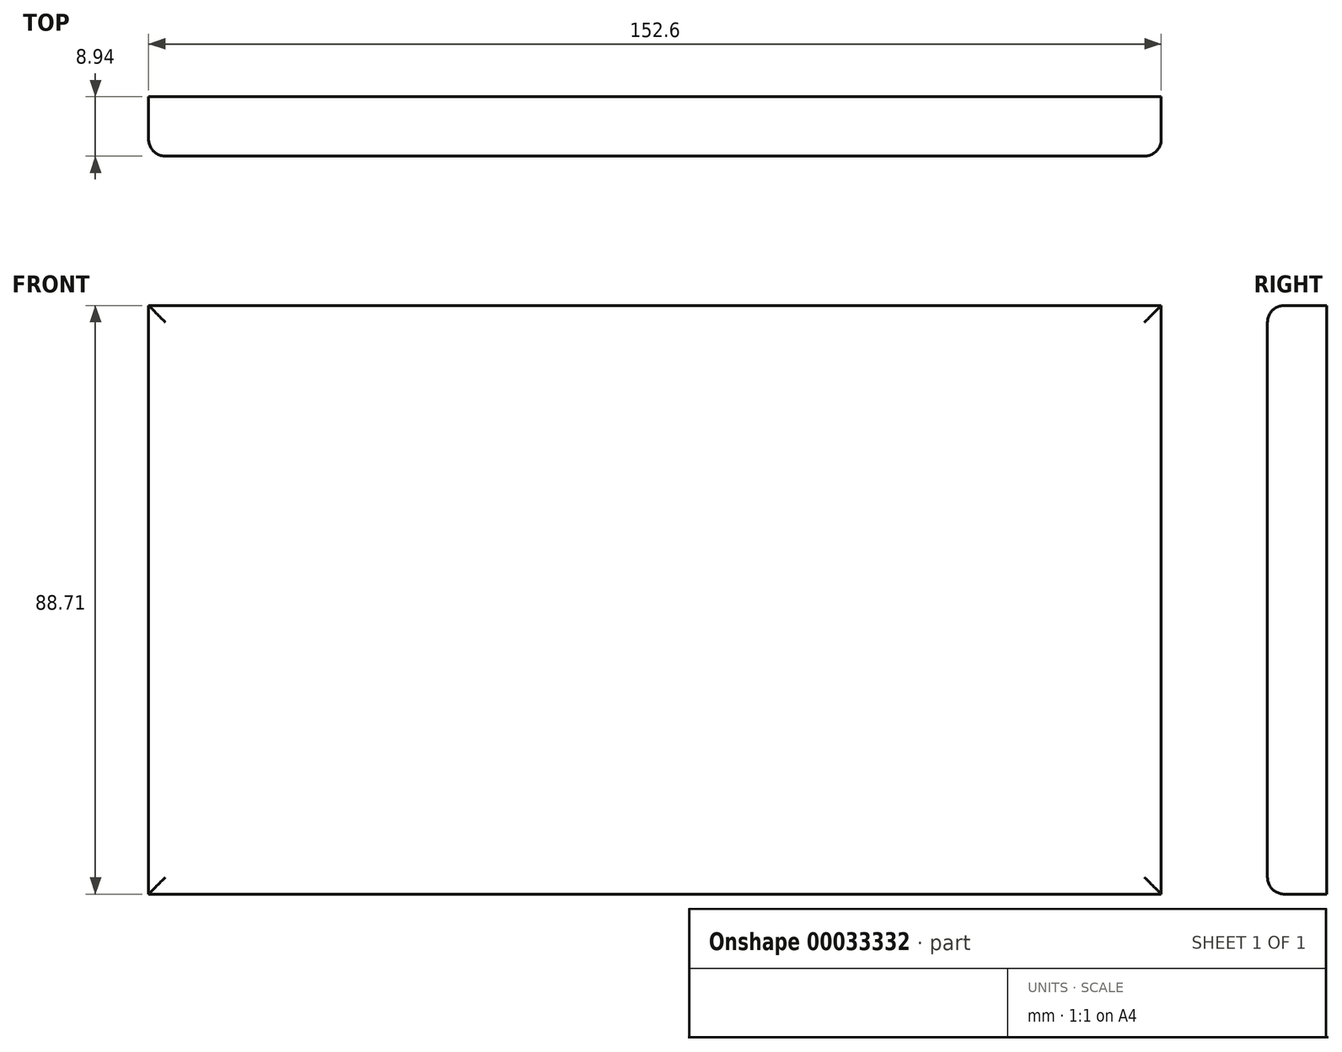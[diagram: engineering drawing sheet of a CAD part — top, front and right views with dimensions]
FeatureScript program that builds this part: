
annotation { "Feature Type Name" : "Feature", "Feature Type Description" : "" }
export const myFeature = defineFeature(function(context is Context, id is Id, definition is map)
    precondition{}
    {
        {
            var Q0;
            Q0=qCreatedBy(makeId("Front.planeOp"),FACE);
            var sketch = newSketch(context, id + "F0", { "sketchPlane" : qUnion([Q0])});
            skLineSegment(sketch, "E0.bottom", {"start": v(-76.44, 47.2) * mm, "end": v(76.16, 47.2) * mm});
            skLineSegment(sketch, "E0.top", {"start": v(-76.44, -41.5) * mm, "end": v(76.16, -41.5) * mm});
            skLineSegment(sketch, "E0.left", {"start": v(-76.44, 47.2) * mm, "end": v(-76.44, -41.5) * mm});
            skLineSegment(sketch, "E0.right", {"start": v(76.16, 47.2) * mm, "end": v(76.16, -41.5) * mm});
            skSolve(sketch);
        }
        {
            var Q0;
            Q0=makeQuery(id+"F0.imprint","IMPRINT",FACE,{"disambiguationData":[TD([[makeQuery(id+"F0.imprint","IMPRINT",EDGE,{"derivedFrom":sQuery(id+"F0.wireOp",EDGE,"E0.bottom")}),-1.0]])]});
            extrude(context, id + "F1", {"entities" : qUnion([Q0]), "depth" : 8.94 * mm});
        }
        {
            var Q0;
            Q0=makeQuery(id+"F1.opExtrude","CAP_FACE",FACE,{"disambiguationData":[OSD([sQuery(id+"F0.wireOp",EDGE,"E0.bottom"),sQuery(id+"F0.wireOp",EDGE,"E0.top"),sQuery(id+"F0.wireOp",EDGE,"E0.left"),sQuery(id+"F0.wireOp",EDGE,"E0.right")])],"isStart":false});
            fillet(context, id + "F2", {"entities" : qUnion([Q0]), "radius" : 2.54 * mm, "tangentPropagation" : true, "allowEdgeOverflow" : false});
        }
    });
